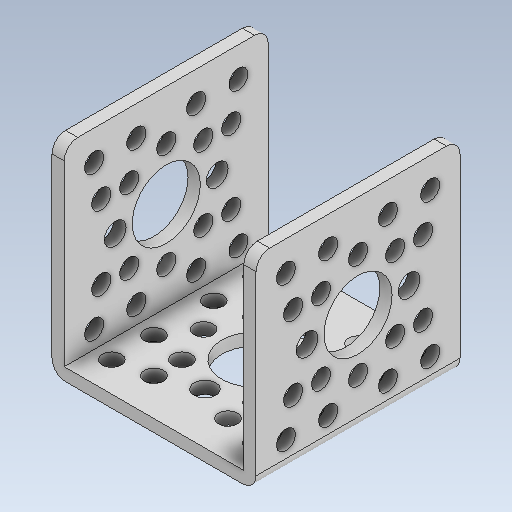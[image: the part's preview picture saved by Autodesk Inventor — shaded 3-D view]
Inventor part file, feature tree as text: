
AUTODESK INVENTOR PART (.ipt)
format: ipt  version: 2020 (Build 240168000, 168)  size: 283,648 bytes
history: native  units: in
note: dims shown in document units (in); Inventor stores cm internally (conversion verified against a paired STEP export)
features: mirror x1
ambient origin geometry x8: Origin, YZ Plane, XZ Plane, XY Plane, X Axis, Y Axis, Z Axis, Center Point
bodies: Solid1 (feature_tree)
feature tree (1):
  mirror  "Mirror9"
